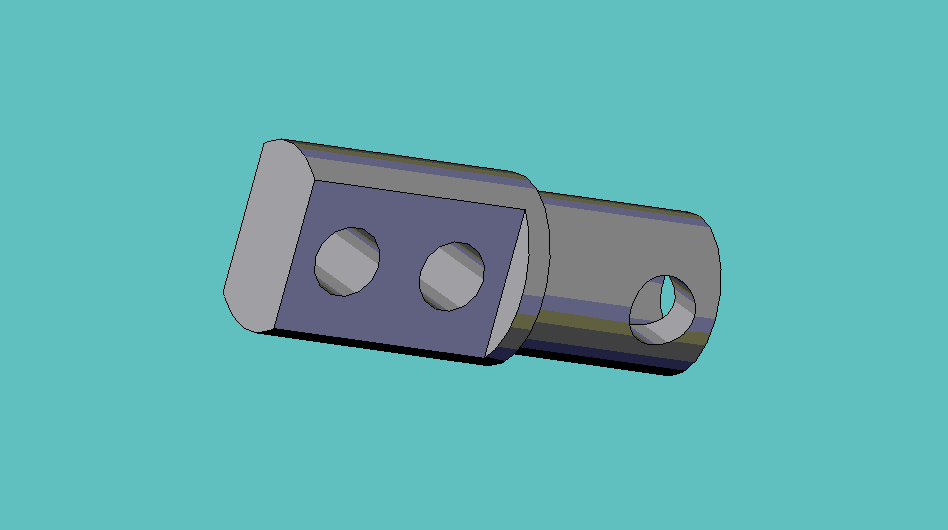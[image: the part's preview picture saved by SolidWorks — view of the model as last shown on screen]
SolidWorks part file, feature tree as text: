
SOLIDWORKS PART (.sldprt)
format: sldprt  version: not decoded by parser v0  size: 129,024 bytes
history: native  units: mm
features: sketch x5, extrude x3, cut_extrude x2, material x1 (+12 scaffold rows collapsed)
feature tree (23):
  scaffold x12  (default folders/planes/origin — collapsed)
  material  "Material <not specified>"
  sketch  "Sketch1"  dims[D1=3.7465mm]
  extrude  "Extrude1"  Depth=17.47mm
  extrude  "Extrude2"  [1 undecoded]
  sketch  "Sketch1<3>"  dims[D1=1.5875mm]
  extrude  "Extrude3"  [1 undecoded]
  sketch  "Sketch1<4>"  dims[D1=13.487mm]
  cut_extrude  "Cut-Extrude1"  [1 undecoded]
  sketch  "Sketch1<5>"  dims[D1=13.487mm]
  sketch  "Sketch2"  dims[D1=26.9875mm]
  cut_extrude  "Cut-Extrude2"  Depth=13.487mm
decode coverage: 7 of 10 modeling features carry decoded parameters
note: 3 parameter values undecoded
summary: no parameter record found for 3 features
note: suppression state not decoded; provenance and decode notes live in map.json
